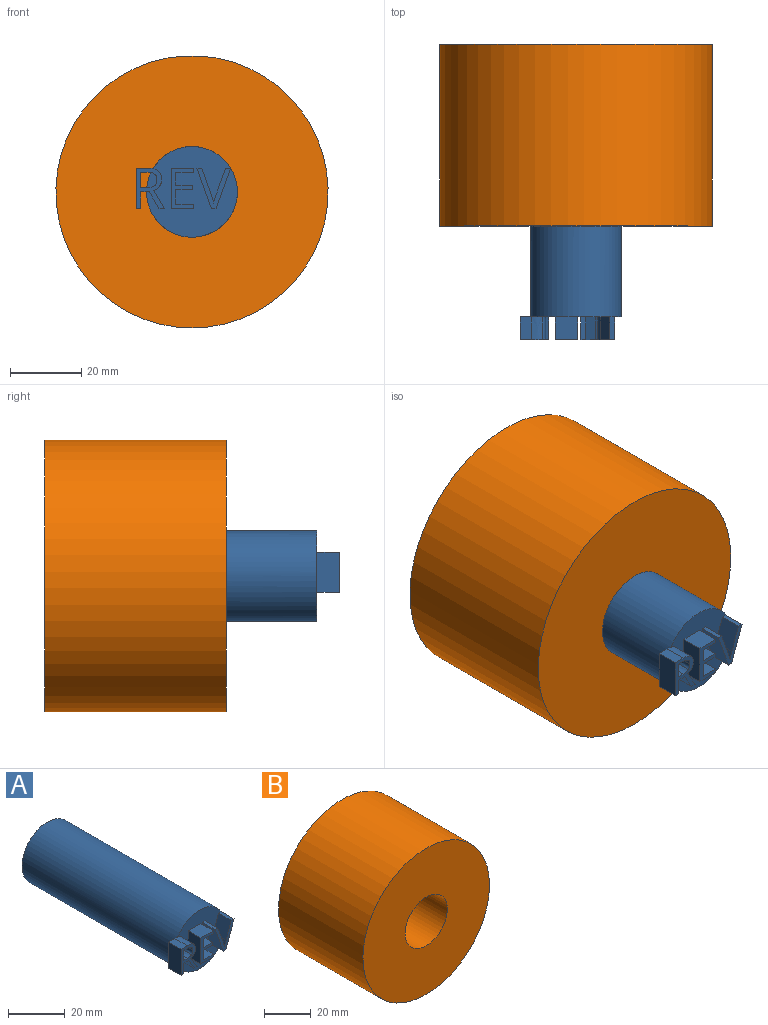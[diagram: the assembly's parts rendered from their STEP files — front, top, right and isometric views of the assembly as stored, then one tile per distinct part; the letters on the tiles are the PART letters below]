
ASSEMBLY  parts=2 mates=1
PART A: 47 faces, bbox 28.3x82.6x25.4 mm
  f0: plane 4.25x2.81mm, normal (0,-1,0), area 8.3mm2, adj f2,f15,f16,f17,f18,f19
  f1: plane 25.4x25.4mm, normal (0,-1,0), area 419mm2, adj f2,f5,f10,f11,f12,f13,f14,f22
  f2: cylinder r=12.7mm len=76.2mm, axis (0,1,0), area 6080.5mm2, adj f0,f1,f3,f4
  f3: plane 25.4x25.4mm, normal (0,1,0), area 506.7mm2, adj f2
  f4: plane 11.29x4.74mm, normal (0,1,0), area 20.3mm2, adj f2,f5,f6,f7,f8,f9,f10,f15
  f5: extruded ~6.35x3.07mm, area 20.5mm2, adj f1,f4,f6,f22,f23
  f6: plane 6.35x3.1mm, normal (0,0,1), area 19.7mm2, adj f4,f5,f7,f23
  f7: plane 11.29x6.35mm, normal (-1,0,0), area 71.7mm2, adj f4,f6,f8,f23
  f8: plane 6.35x1.31mm, normal (0,0,-1), area 8.3mm2, adj f4,f7,f9,f23
  f9: plane 6.35x4.7mm, normal (1,0,0), area 29.8mm2, adj f4,f8,f10,f23
  f10: plane 6.35x2.36mm, normal (0,0,-1), area 15mm2, adj f1,f4,f9,f11,f23
  f11: plane 6.35x4.7mm, normal (-0.86,0,-0.5), area 34.5mm2, adj f1,f10,f12,f23
  f12: plane 6.35x1.55mm, normal (0,0,-1), area 9.9mm2, adj f1,f11,f13,f23
  f13: plane 6.35x5.07mm, normal (0.86,0,0.52), area 37.6mm2, adj f1,f12,f14,f23
  f14: extruded ~6.35x3.03mm, area 25.9mm2, adj f1,f13,f22,f23
  f15: extruded ~6.35x2.12mm, area 14mm2, adj f0,f4,f16,f21,f23
  f16: extruded ~6.35x1.61mm, area 11.5mm2, adj f0,f15,f17,f23
  f17: extruded ~6.35x1.66mm, area 11.7mm2, adj f0,f16,f18,f23
  f18: extruded ~6.35x2.04mm, area 13.7mm2, adj f0,f17,f19,f23
  f19: plane 6.35x1.8mm, normal (0,0,1), area 11.4mm2, adj f0,f4,f18,f20,f23
  f20: plane 6.35x4.32mm, normal (1,0,0), area 27.4mm2, adj f4,f19,f21,f23
  f21: plane 6.35x1.71mm, normal (0,0,-1), area 10.8mm2, adj f4,f15,f20,f23
  f22: extruded ~6.35x2.39mm, area 17.1mm2, adj f1,f5,f14,f23
  f23: plane 11.29x7.95mm, normal (0,-1,0), area 38.2mm2, adj f5,f6,f7,f8,f9,f10,f11,f12
  f24: plane 6.35x6.29mm, normal (0,0,-1), area 40mm2, adj f1,f25,f35,f36
  f25: plane 6.35x1.17mm, normal (1,0,0), area 7.5mm2, adj f1,f24,f26,f36
  f26: plane 6.35x4.98mm, normal (0,0,1), area 31.6mm2, adj f1,f25,f27,f36
  f27: plane 6.35x4.15mm, normal (1,0,0), area 26.4mm2, adj f1,f26,f28,f36
  f28: plane 6.35x4.68mm, normal (0,0,-1), area 29.7mm2, adj f1,f27,f29,f36
  f29: plane 6.35x1.16mm, normal (1,0,0), area 7.4mm2, adj f1,f28,f30,f36
  f30: plane 6.35x4.68mm, normal (0,0,1), area 29.7mm2, adj f1,f29,f31,f36
  f31: plane 6.35x3.64mm, normal (1,0,0), area 23.1mm2, adj f1,f30,f32,f36
  f32: plane 6.35x4.98mm, normal (0,0,-1), area 31.6mm2, adj f1,f31,f33,f36
  f33: plane 6.35x1.17mm, normal (1,0,0), area 7.4mm2, adj f1,f32,f34,f36
  f34: plane 6.35x6.29mm, normal (0,0,1), area 40mm2, adj f1,f33,f35,f36
  f35: plane 11.29x6.35mm, normal (-1,0,0), area 71.7mm2, adj f1,f24,f34,f36
  f36: plane 11.29x6.29mm, normal (0,-1,0), area 31.9mm2, adj f24,f25,f26,f27,f28,f29,f30,f31
  f37: plane 6.35x1.41mm, normal (0,0,1), area 9mm2, adj f1,f38,f45,f46
  f38: plane 7.26x6.35mm, normal (-0.94,0,0.33), area 48.9mm2, adj f1,f37,f39,f46
  f39: extruded ~6.35x2.49mm, area 16.5mm2, adj f1,f38,f40,f46
  f40: extruded ~6.35x2.45mm, area 16.2mm2, adj f1,f39,f41,f46
  f41: plane 7.31x6.35mm, normal (0.94,0,0.33), area 49.2mm2, adj f1,f40,f42,f46
  f42: plane 6.35x1.39mm, normal (0,0,1), area 8.8mm2, adj f1,f41,f43,f46
  f43: plane 11.29x6.35mm, normal (-0.94,0,-0.34), area 76.2mm2, adj f1,f42,f44,f46
  f44: plane 6.35x1.3mm, normal (0,0,-1), area 8.2mm2, adj f1,f43,f45,f46
  f45: plane 11.29x6.35mm, normal (0.94,0,-0.34), area 76.2mm2, adj f1,f37,f44,f46
  f46: plane 11.29x9.41mm, normal (0,-1,0), area 29.5mm2, adj f37,f38,f39,f40,f41,f42,f43,f44
PART B: 4 faces, bbox 76.2x50.8x76.2 mm
  f0: cylinder r=38.1mm len=76.2mm, axis (0,1,0), area 12161mm2, adj f1,f2
  f1: plane 76.2x76.2mm, normal (0,-1,0), area 4053.7mm2, adj f0,f3
  f2: plane 76.2x76.2mm, normal (0,1,0), area 4053.7mm2, adj f0,f3
  f3: cylinder r=12.7mm len=50.8mm, axis (0,-1,0), area 4053.7mm2, adj f1,f2
PLACE A t=(-6.2,-6.21,-46.84)mm
PLACE B t=(-12.68,-6.21,-43.76)mm
MATE revolute A.f2 <-> B.f0  axis (0,1,0) through (-36.27,-6.21,-16.01)mm
